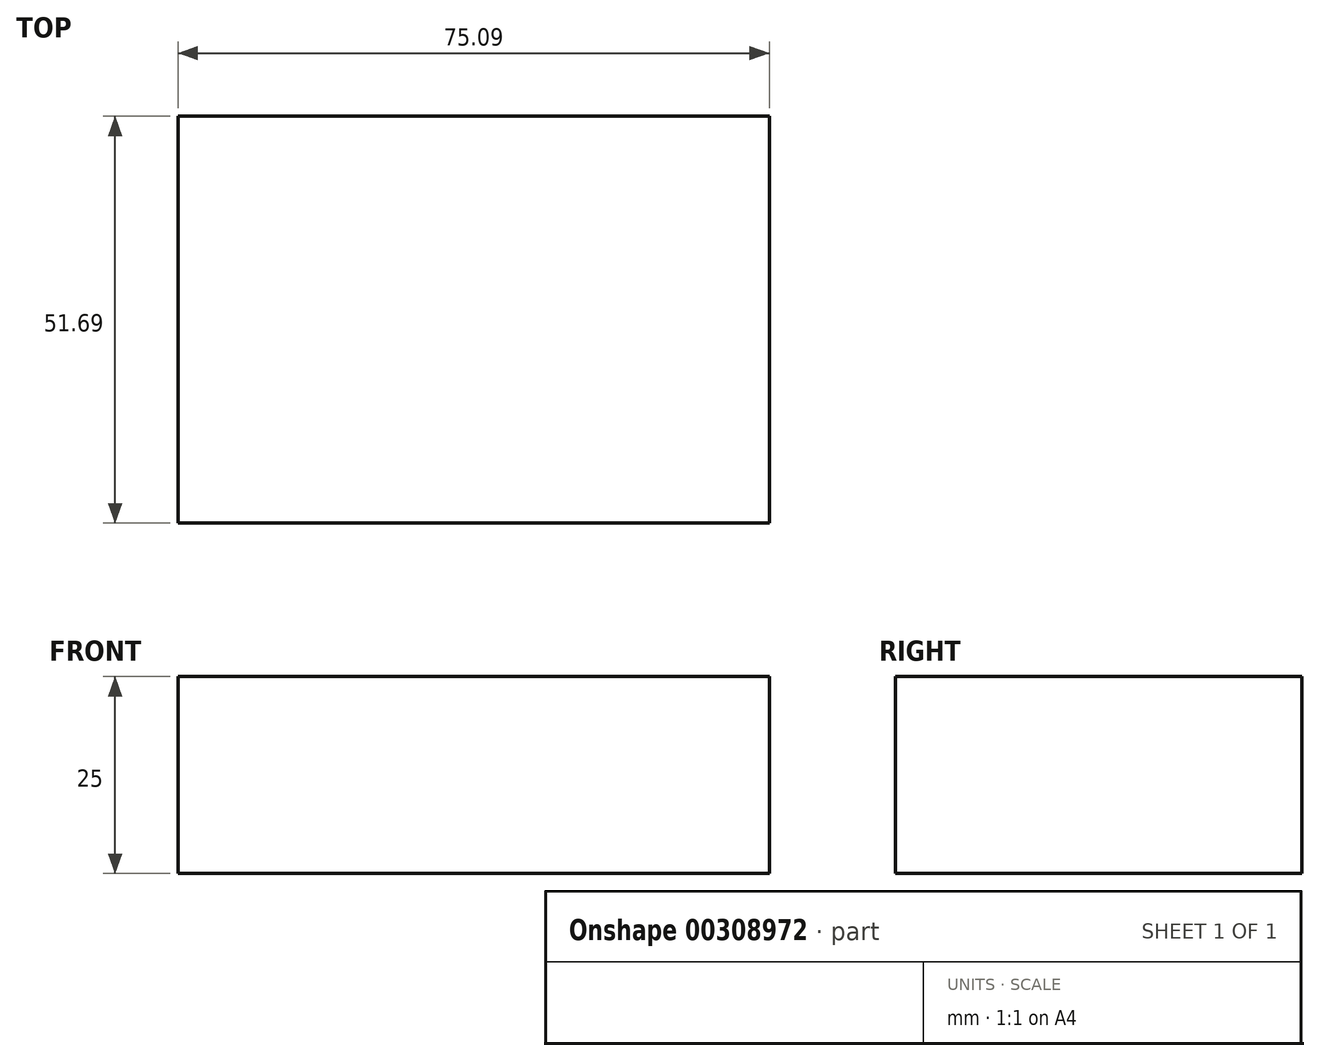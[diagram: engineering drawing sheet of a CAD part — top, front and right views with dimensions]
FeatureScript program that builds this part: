
annotation { "Feature Type Name" : "Feature", "Feature Type Description" : "" }
export const myFeature = defineFeature(function(context is Context, id is Id, definition is map)
    precondition{}
    {
        {
            var Q0;
            Q0=qCreatedBy(makeId("Top.planeOp"),FACE);
            var sketch = newSketch(context, id + "F0", { "sketchPlane" : qUnion([Q0])});
            skLineSegment(sketch, "E0.bottom", {"start": v(-104.64, 21.05) * mm, "end": v(-29.55, 21.05) * mm});
            skLineSegment(sketch, "E0.top", {"start": v(-104.64, -30.64) * mm, "end": v(-29.55, -30.64) * mm});
            skLineSegment(sketch, "E0.left", {"start": v(-104.64, 21.05) * mm, "end": v(-104.64, -30.64) * mm});
            skLineSegment(sketch, "E0.right", {"start": v(-29.55, 21.05) * mm, "end": v(-29.55, -30.64) * mm});
            skSolve(sketch);
        }
        {
            var Q0;
            Q0=makeQuery(id+"F0.imprint","IMPRINT",FACE,{"disambiguationData":[TD([[makeQuery(id+"F0.imprint","IMPRINT",EDGE,{"derivedFrom":sQuery(id+"F0.wireOp",EDGE,"E0.bottom")}),-1.0]])]});
            extrude(context, id + "F1", {"entities" : qUnion([Q0]), "depth" : 25 * mm});
        }
    });
